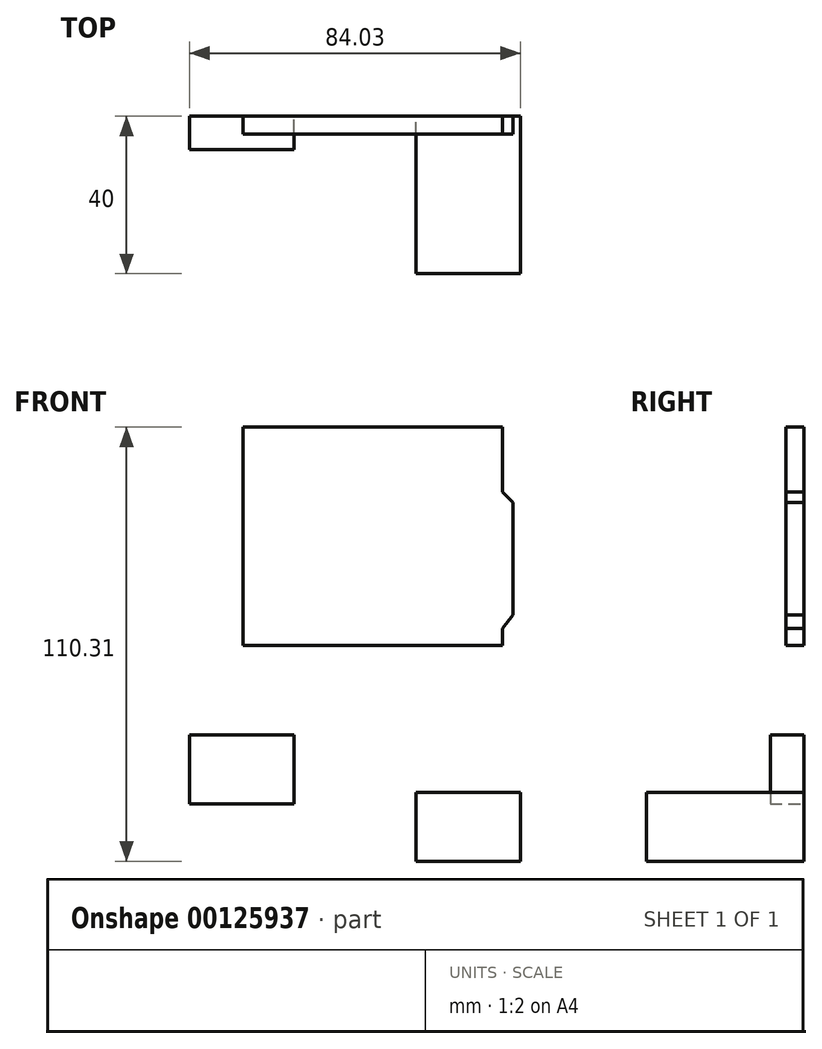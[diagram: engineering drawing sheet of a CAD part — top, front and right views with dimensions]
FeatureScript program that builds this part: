
annotation { "Feature Type Name" : "Feature", "Feature Type Description" : "" }
export const myFeature = defineFeature(function(context is Context, id is Id, definition is map)
    precondition{}
    {
        {
            var Q0;
            Q0=qCreatedBy(makeId("Front.planeOp"),FACE);
            var sketch = newSketch(context, id + "F0", { "sketchPlane" : qUnion([Q0])});
            skLineSegment(sketch, "E0", {"start": v(-48.3, 0) * mm, "end": v(17.7, 0) * mm});
            skLineSegment(sketch, "E1", {"start": v(17.7, 0) * mm, "end": v(17.7, 4.42) * mm});
            skLineSegment(sketch, "E2", {"start": v(17.7, 4.42) * mm, "end": v(20.28, 7.84) * mm});
            skLineSegment(sketch, "E3", {"start": v(20.28, 7.84) * mm, "end": v(20.28, 36.4) * mm});
            skLineSegment(sketch, "E4", {"start": v(20.28, 36.4) * mm, "end": v(17.7, 39.02) * mm});
            skLineSegment(sketch, "E5", {"start": v(17.7, 39.02) * mm, "end": v(17.7, 55.5) * mm});
            skLineSegment(sketch, "E6", {"start": v(17.7, 55.5) * mm, "end": v(-48.3, 55.5) * mm});
            skLineSegment(sketch, "E7", {"start": v(-48.3, 55.5) * mm, "end": v(-48.3, 0) * mm});
            skSolve(sketch);
        }
        {
            var Q0;
            Q0=qSketchRegion(id+"F0",true);
            extrude(context, id + "F1", {"entities" : qUnion([Q0]), "depth" : 4.54 * mm});
        }
        {
            var Q0;
            Q0=qCreatedBy(makeId("Front.planeOp"),FACE);
            var sketch = newSketch(context, id + "F2", { "sketchPlane" : qUnion([Q0])});
            skLineSegment(sketch, "E8.bottom", {"start": v(-4.28, -37.3) * mm, "end": v(22.22, -37.3) * mm});
            skLineSegment(sketch, "E8.top", {"start": v(-4.28, -54.8) * mm, "end": v(22.22, -54.8) * mm});
            skLineSegment(sketch, "E8.left", {"start": v(-4.28, -37.3) * mm, "end": v(-4.28, -54.8) * mm});
            skLineSegment(sketch, "E8.right", {"start": v(22.22, -37.3) * mm, "end": v(22.22, -54.8) * mm});
            skSolve(sketch);
        }
        {
            var Q0;
            Q0=qSketchRegion(id+"F2",true);
            extrude(context, id + "F3", {"entities" : qUnion([Q0]), "depth" : 40 * mm});
        }
        {
            var Q0;
            Q0=qCreatedBy(makeId("Front.planeOp"),FACE);
            var sketch = newSketch(context, id + "F4", { "sketchPlane" : qUnion([Q0])});
            skLineSegment(sketch, "E9.bottom", {"start": v(-61.8, -22.69) * mm, "end": v(-35.3, -22.69) * mm});
            skLineSegment(sketch, "E9.top", {"start": v(-61.8, -40.19) * mm, "end": v(-35.3, -40.19) * mm});
            skLineSegment(sketch, "E9.left", {"start": v(-61.8, -22.69) * mm, "end": v(-61.8, -40.19) * mm});
            skLineSegment(sketch, "E9.right", {"start": v(-35.3, -22.69) * mm, "end": v(-35.3, -40.19) * mm});
            skSolve(sketch);
        }
        {
            var Q0;
            Q0=qSketchRegion(id+"F4",true);
            extrude(context, id + "F5", {"entities" : qUnion([Q0]), "depth" : 8.5 * mm});
        }
    });
